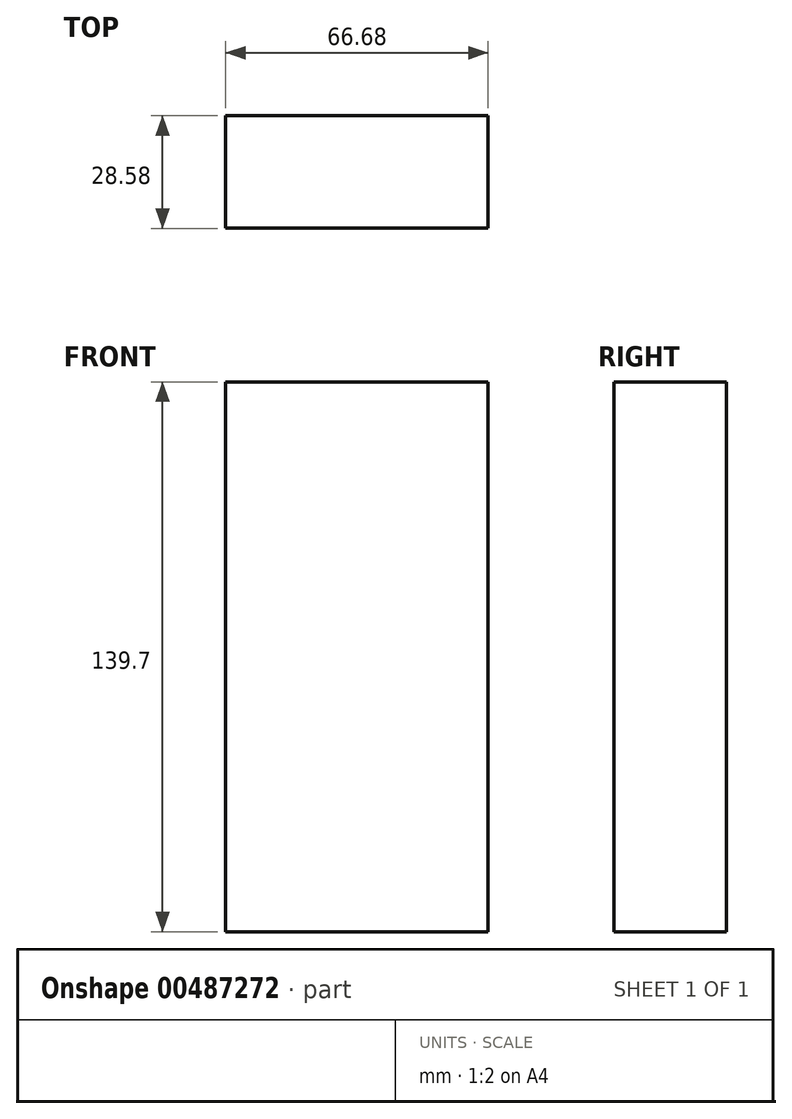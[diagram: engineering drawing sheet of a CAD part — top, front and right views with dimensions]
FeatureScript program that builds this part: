
annotation { "Feature Type Name" : "Feature", "Feature Type Description" : "" }
export const myFeature = defineFeature(function(context is Context, id is Id, definition is map)
    precondition{}
    {
        {
            var Q0;
            Q0=qCreatedBy(makeId("Top.planeOp"),FACE);
            var sketch = newSketch(context, id + "F0", { "sketchPlane" : qUnion([Q0])});
            skLineSegment(sketch, "E0.bottom", {"start": v(-33.34, 14.29) * mm, "end": v(33.34, 14.29) * mm});
            skLineSegment(sketch, "E0.top", {"start": v(-33.34, -14.29) * mm, "end": v(33.34, -14.29) * mm});
            skLineSegment(sketch, "E0.left", {"start": v(-33.34, 14.29) * mm, "end": v(-33.34, -14.29) * mm});
            skLineSegment(sketch, "E0.right", {"start": v(33.34, 14.29) * mm, "end": v(33.34, -14.29) * mm});
            skLineSegment(sketch, "E1", {"start": v(-33.34, 14.29) * mm, "end": v(33.34, -14.29) * mm, "construction": true});
            skSolve(sketch);
        }
        {
            var Q0;
            Q0 = qSketchRegion(id + "F0", true);
            extrude(context, id + "F1", {"entities" : qUnion([Q0]), "depth" : 139.7 * mm, "symmetric" : true});
        }
    });
